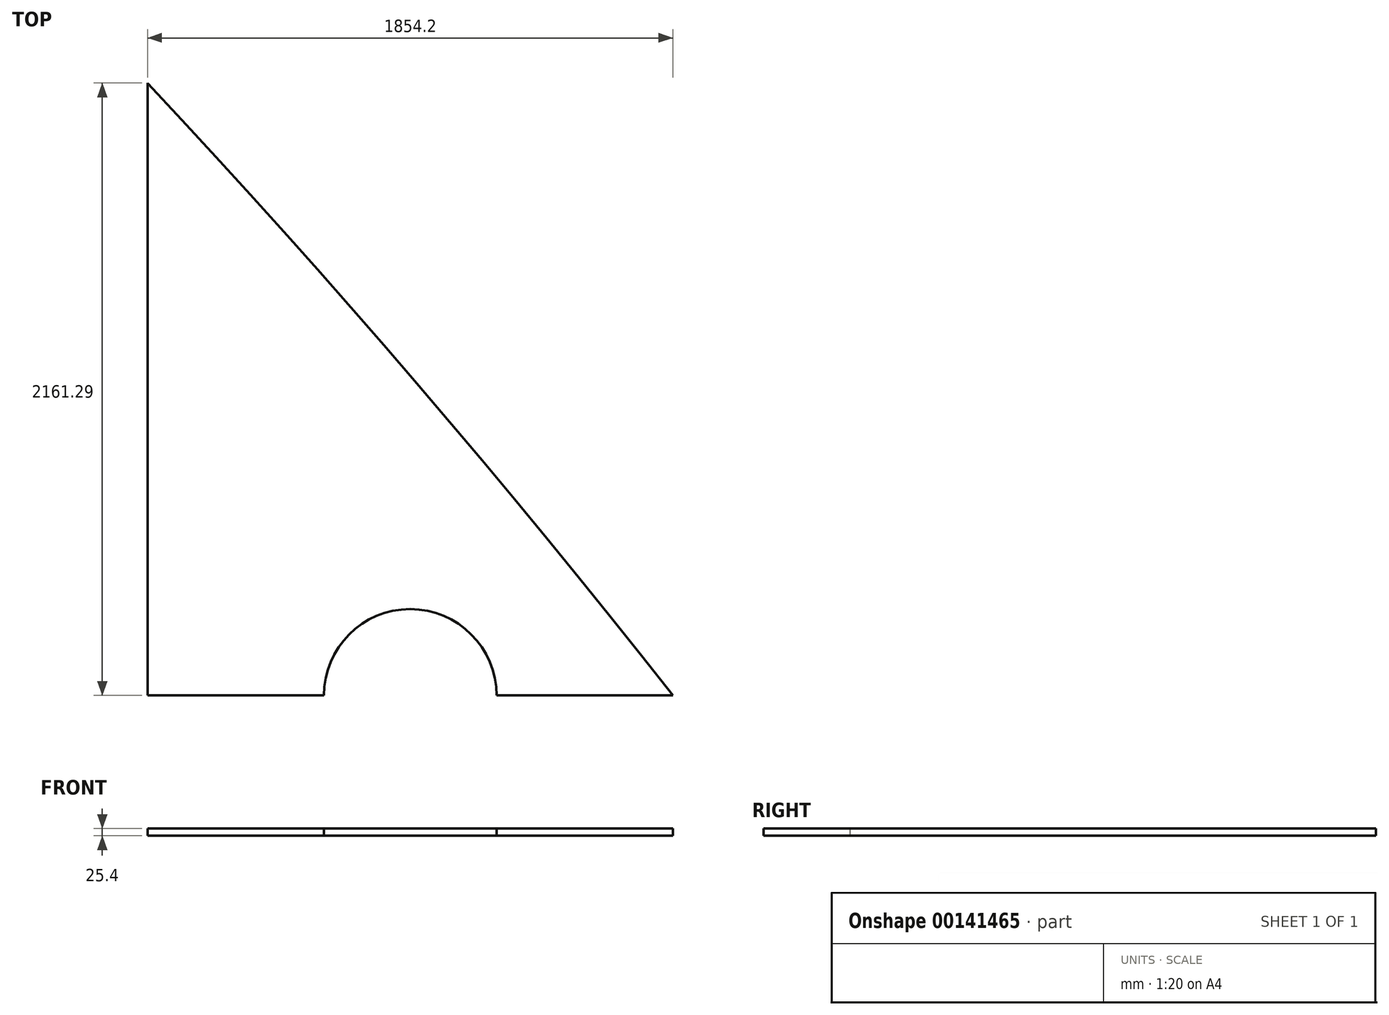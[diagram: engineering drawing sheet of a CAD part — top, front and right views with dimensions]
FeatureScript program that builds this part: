
annotation { "Feature Type Name" : "Feature", "Feature Type Description" : "" }
export const myFeature = defineFeature(function(context is Context, id is Id, definition is map)
    precondition{}
    {
        {
            var Q0;
            Q0=qCreatedBy(makeId("Top.planeOp"),FACE);
            var sketch = newSketch(context, id + "F0", { "sketchPlane" : qUnion([Q0])});
            skLineSegment(sketch, "E0", {"start": v(-963.17, 1967.51) * mm, "end": v(-340.87, 1967.51) * mm});
            skLineSegment(sketch, "E1", {"start": v(-963.17, 1967.51) * mm, "end": v(-963.17, 4128.8) * mm});
            skLineSegment(sketch, "E2", {"start": v(891.03, 1967.51) * mm, "end": v(891.03, 1967.51) * mm});
            skLineSegment(sketch, "E3", {"start": v(-36.07, 2272.31) * mm, "end": v(-36.07, 3096.04) * mm});
            skArc(sketch, "E4", {"start": v(891.03, 1967.51) * mm, "mid": v(-12.4, 3068.47) * mm, "end": v(-963.17, 4128.8) * mm});
            skArc(sketch, "E5", {"start": v(268.73, 1967.51) * mm, "mid": v(-36.07, 2272.31) * mm, "end": v(-340.87, 1967.51) * mm});
            skLineSegment(sketch, "E6.trimOffspring", {"start": v(268.73, 1967.51) * mm, "end": v(891.03, 1967.51) * mm});
            skSolve(sketch);
        }
        {
            var Q0;
            {var subQ3=sQuery(id+"F0.wireOp",EDGE,"E0");Q0=makeQuery(id+"F0.imprint","IMPRINT",FACE,{"disambiguationData":[TD([[makeQuery(id+"F0.imprint","IMPRINT",EDGE,{"derivedFrom":subQ3}),1.0]])]});}
            var Q1;
            {var subQ0=sQuery(id+"F0.wireOp",EDGE,"E3");Q1=makeQuery(id+"F0.imprint","IMPRINT",FACE,{"disambiguationData":[TD([[makeQuery(id+"F0.imprint","IMPRINT",EDGE,{"derivedFrom":subQ0}),-1.0]])]});}
            extrude(context, id + "F1", {"entities" : qUnion([Q0, Q1]), "depth" : 25.4 * mm});
        }
    });
